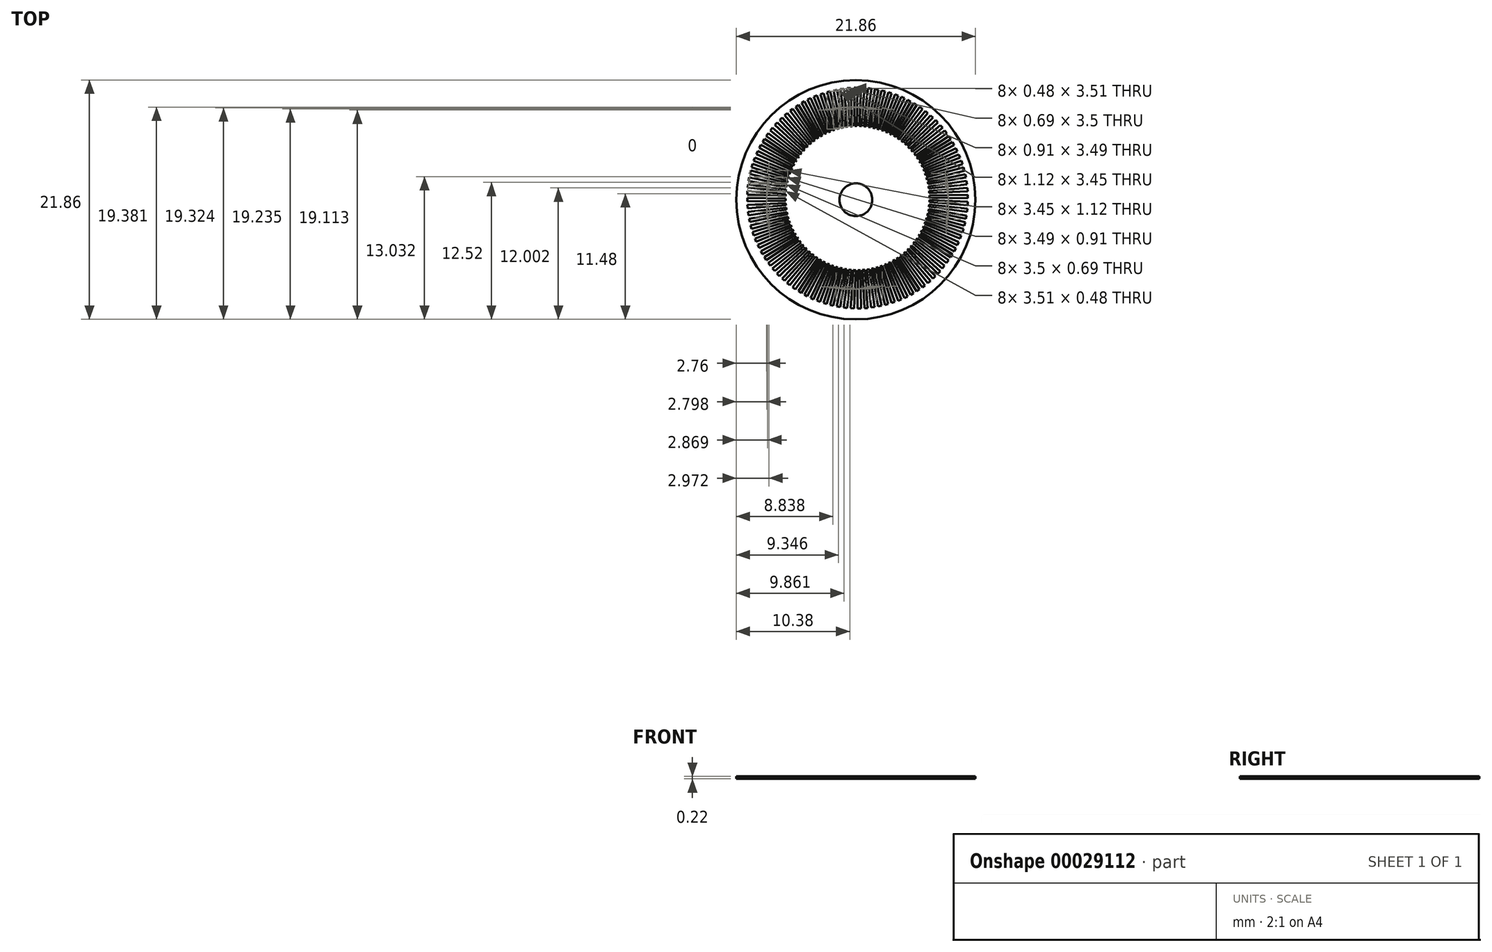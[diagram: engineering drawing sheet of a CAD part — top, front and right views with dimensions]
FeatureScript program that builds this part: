
annotation { "Feature Type Name" : "Feature", "Feature Type Description" : "" }
export const myFeature = defineFeature(function(context is Context, id is Id, definition is map)
    precondition{}
    {
        {
            var Q0;
            Q0=qCreatedBy(makeId("Top.planeOp"),FACE);
            var sketch = newSketch(context, id + "F0", { "sketchPlane" : qUnion([Q0])});
            skCircle(sketch, "E0", {"center": v(0, 0) * mm, "radius": 1.5 * mm});
            skCircle(sketch, "E1", {"center": v(0, 0) * mm, "radius": 10.93 * mm});
            skLineSegment(sketch, "E2", {"start": v(-0.16, 10.23) * mm, "end": v(0.16, 10.23) * mm});
            skLineSegment(sketch, "E3", {"start": v(-0.1, 6.73) * mm, "end": v(0.1, 6.73) * mm});
            skLineSegment(sketch, "E4.trimOffspring", {"start": v(0.1, 6.73) * mm, "end": v(0.16, 10.23) * mm});
            skLineSegment(sketch, "E5.trimOffspring", {"start": v(-0.1, 6.73) * mm, "end": v(-0.16, 10.23) * mm});
            skLineSegment(sketch, "E6.1.0", {"start": v(-0.79, 10.19) * mm, "end": v(-0.48, 10.2) * mm});
            skLineSegment(sketch, "E6.1.1", {"start": v(-0.31, 6.7) * mm, "end": v(-0.48, 10.2) * mm});
            skLineSegment(sketch, "E6.1.2", {"start": v(-0.51, 6.7) * mm, "end": v(-0.79, 10.19) * mm});
            skLineSegment(sketch, "E6.1.3", {"start": v(-0.51, 6.7) * mm, "end": v(-0.31, 6.7) * mm});
            skLineSegment(sketch, "E6.2.0", {"start": v(-1.42, 10.1) * mm, "end": v(-1.1, 10.15) * mm});
            skLineSegment(sketch, "E6.2.1", {"start": v(-0.72, 6.67) * mm, "end": v(-1.1, 10.15) * mm});
            skLineSegment(sketch, "E6.2.2", {"start": v(-0.92, 6.64) * mm, "end": v(-1.42, 10.1) * mm});
            skLineSegment(sketch, "E6.2.3", {"start": v(-0.92, 6.64) * mm, "end": v(-0.72, 6.67) * mm});
            skLineSegment(sketch, "E6.3.0", {"start": v(-2.04, 9.99) * mm, "end": v(-1.73, 10.05) * mm});
            skLineSegment(sketch, "E6.3.1", {"start": v(-1.13, 6.6) * mm, "end": v(-1.73, 10.05) * mm});
            skLineSegment(sketch, "E6.3.2", {"start": v(-1.33, 6.56) * mm, "end": v(-2.04, 9.99) * mm});
            skLineSegment(sketch, "E6.3.3", {"start": v(-1.33, 6.56) * mm, "end": v(-1.13, 6.6) * mm});
            skLineSegment(sketch, "E6.4.0", {"start": v(-2.65, 9.83) * mm, "end": v(-2.35, 9.9) * mm});
            skLineSegment(sketch, "E6.4.1", {"start": v(-1.53, 6.5) * mm, "end": v(-2.35, 9.9) * mm});
            skLineSegment(sketch, "E6.4.2", {"start": v(-1.73, 6.46) * mm, "end": v(-2.65, 9.83) * mm});
            skLineSegment(sketch, "E6.4.3", {"start": v(-1.73, 6.46) * mm, "end": v(-1.53, 6.5) * mm});
            skLineSegment(sketch, "E6.5.0", {"start": v(-3.25, 9.64) * mm, "end": v(-2.96, 9.73) * mm});
            skLineSegment(sketch, "E6.5.1", {"start": v(-1.93, 6.39) * mm, "end": v(-2.96, 9.73) * mm});
            skLineSegment(sketch, "E6.5.2", {"start": v(-2.12, 6.33) * mm, "end": v(-3.25, 9.64) * mm});
            skLineSegment(sketch, "E6.5.3", {"start": v(-2.12, 6.33) * mm, "end": v(-1.93, 6.39) * mm});
            skLineSegment(sketch, "E6.6.0", {"start": v(-3.84, 9.4) * mm, "end": v(-3.55, 9.52) * mm});
            skLineSegment(sketch, "E6.6.1", {"start": v(-2.32, 6.25) * mm, "end": v(-3.55, 9.52) * mm});
            skLineSegment(sketch, "E6.6.2", {"start": v(-2.5, 6.17) * mm, "end": v(-3.84, 9.4) * mm});
            skLineSegment(sketch, "E6.6.3", {"start": v(-2.5, 6.17) * mm, "end": v(-2.32, 6.25) * mm});
            skLineSegment(sketch, "E6.7.0", {"start": v(-4.42, 9.14) * mm, "end": v(-4.13, 9.27) * mm});
            skLineSegment(sketch, "E6.7.1", {"start": v(-2.7, 6.08) * mm, "end": v(-4.13, 9.27) * mm});
            skLineSegment(sketch, "E6.7.2", {"start": v(-2.88, 6) * mm, "end": v(-4.42, 9.14) * mm});
            skLineSegment(sketch, "E6.7.3", {"start": v(-2.88, 6) * mm, "end": v(-2.7, 6.08) * mm});
            skLineSegment(sketch, "E6.8.0", {"start": v(-4.97, 8.83) * mm, "end": v(-4.7, 8.98) * mm});
            skLineSegment(sketch, "E6.8.1", {"start": v(-3.06, 5.89) * mm, "end": v(-4.7, 8.98) * mm});
            skLineSegment(sketch, "E6.8.2", {"start": v(-3.24, 5.8) * mm, "end": v(-4.97, 8.83) * mm});
            skLineSegment(sketch, "E6.8.3", {"start": v(-3.24, 5.8) * mm, "end": v(-3.06, 5.89) * mm});
            skLineSegment(sketch, "E6.9.0", {"start": v(-5.5, 8.5) * mm, "end": v(-5.24, 8.66) * mm});
            skLineSegment(sketch, "E6.9.1", {"start": v(-3.41, 5.68) * mm, "end": v(-5.24, 8.66) * mm});
            skLineSegment(sketch, "E6.9.2", {"start": v(-3.58, 5.57) * mm, "end": v(-5.5, 8.5) * mm});
            skLineSegment(sketch, "E6.9.3", {"start": v(-3.58, 5.57) * mm, "end": v(-3.41, 5.68) * mm});
            skLineSegment(sketch, "E6.10.0", {"start": v(-6.02, 8.12) * mm, "end": v(-5.77, 8.3) * mm});
            skLineSegment(sketch, "E6.10.1", {"start": v(-3.75, 5.44) * mm, "end": v(-5.77, 8.3) * mm});
            skLineSegment(sketch, "E6.10.2", {"start": v(-3.92, 5.32) * mm, "end": v(-6.02, 8.12) * mm});
            skLineSegment(sketch, "E6.10.3", {"start": v(-3.92, 5.32) * mm, "end": v(-3.75, 5.44) * mm});
            skLineSegment(sketch, "E6.11.0", {"start": v(-6.5, 7.72) * mm, "end": v(-6.27, 7.92) * mm});
            skLineSegment(sketch, "E6.11.1", {"start": v(-4.08, 5.18) * mm, "end": v(-6.27, 7.92) * mm});
            skLineSegment(sketch, "E6.11.2", {"start": v(-4.23, 5.06) * mm, "end": v(-6.5, 7.72) * mm});
            skLineSegment(sketch, "E6.11.3", {"start": v(-4.23, 5.06) * mm, "end": v(-4.08, 5.18) * mm});
            skLineSegment(sketch, "E6.12.0", {"start": v(-6.97, 7.28) * mm, "end": v(-6.74, 7.5) * mm});
            skLineSegment(sketch, "E6.12.1", {"start": v(-4.39, 4.9) * mm, "end": v(-6.74, 7.5) * mm});
            skLineSegment(sketch, "E6.12.2", {"start": v(-4.53, 4.77) * mm, "end": v(-6.97, 7.28) * mm});
            skLineSegment(sketch, "E6.12.3", {"start": v(-4.53, 4.77) * mm, "end": v(-4.39, 4.9) * mm});
            skLineSegment(sketch, "E6.13.0", {"start": v(-7.4, 6.82) * mm, "end": v(-7.2, 7.05) * mm});
            skLineSegment(sketch, "E6.13.1", {"start": v(-4.68, 4.62) * mm, "end": v(-7.2, 7.05) * mm});
            skLineSegment(sketch, "E6.13.2", {"start": v(-4.81, 4.47) * mm, "end": v(-7.4, 6.82) * mm});
            skLineSegment(sketch, "E6.13.3", {"start": v(-4.81, 4.47) * mm, "end": v(-4.68, 4.62) * mm});
            skLineSegment(sketch, "E6.14.0", {"start": v(-7.8, 6.34) * mm, "end": v(-7.6, 6.58) * mm});
            skLineSegment(sketch, "E6.14.1", {"start": v(-4.95, 4.3) * mm, "end": v(-7.6, 6.58) * mm});
            skLineSegment(sketch, "E6.14.2", {"start": v(-5.08, 4.15) * mm, "end": v(-7.8, 6.34) * mm});
            skLineSegment(sketch, "E6.14.3", {"start": v(-5.08, 4.15) * mm, "end": v(-4.95, 4.3) * mm});
            skLineSegment(sketch, "E6.15.0", {"start": v(-8.18, 5.82) * mm, "end": v(-8, 6.08) * mm});
            skLineSegment(sketch, "E6.15.1", {"start": v(-5.2, 3.97) * mm, "end": v(-8, 6.08) * mm});
            skLineSegment(sketch, "E6.15.2", {"start": v(-5.32, 3.81) * mm, "end": v(-8.18, 5.82) * mm});
            skLineSegment(sketch, "E6.15.3", {"start": v(-5.32, 3.81) * mm, "end": v(-5.2, 3.97) * mm});
            skLineSegment(sketch, "E6.16.0", {"start": v(-8.52, 5.3) * mm, "end": v(-8.35, 5.55) * mm});
            skLineSegment(sketch, "E6.16.1", {"start": v(-5.43, 3.63) * mm, "end": v(-8.35, 5.55) * mm});
            skLineSegment(sketch, "E6.16.2", {"start": v(-5.54, 3.46) * mm, "end": v(-8.52, 5.3) * mm});
            skLineSegment(sketch, "E6.16.3", {"start": v(-5.54, 3.46) * mm, "end": v(-5.43, 3.63) * mm});
            skLineSegment(sketch, "E6.17.0", {"start": v(-8.83, 4.74) * mm, "end": v(-8.68, 5) * mm});
            skLineSegment(sketch, "E6.17.1", {"start": v(-5.64, 3.27) * mm, "end": v(-8.68, 5) * mm});
            skLineSegment(sketch, "E6.17.2", {"start": v(-5.73, 3.1) * mm, "end": v(-8.83, 4.74) * mm});
            skLineSegment(sketch, "E6.17.3", {"start": v(-5.73, 3.1) * mm, "end": v(-5.64, 3.27) * mm});
            skLineSegment(sketch, "E6.18.0", {"start": v(-9.1, 4.16) * mm, "end": v(-8.96, 4.45) * mm});
            skLineSegment(sketch, "E6.18.1", {"start": v(-5.82, 2.9) * mm, "end": v(-8.96, 4.45) * mm});
            skLineSegment(sketch, "E6.18.2", {"start": v(-5.9, 2.72) * mm, "end": v(-9.1, 4.16) * mm});
            skLineSegment(sketch, "E6.18.3", {"start": v(-5.9, 2.72) * mm, "end": v(-5.82, 2.9) * mm});
            skLineSegment(sketch, "E6.19.0", {"start": v(-9.33, 3.57) * mm, "end": v(-9.22, 3.86) * mm});
            skLineSegment(sketch, "E6.19.1", {"start": v(-5.98, 2.52) * mm, "end": v(-9.22, 3.86) * mm});
            skLineSegment(sketch, "E6.19.2", {"start": v(-6.06, 2.34) * mm, "end": v(-9.33, 3.57) * mm});
            skLineSegment(sketch, "E6.19.3", {"start": v(-6.06, 2.34) * mm, "end": v(-5.98, 2.52) * mm});
            skLineSegment(sketch, "E6.20.0", {"start": v(-9.53, 2.97) * mm, "end": v(-9.43, 3.27) * mm});
            skLineSegment(sketch, "E6.20.1", {"start": v(-6.12, 2.14) * mm, "end": v(-9.43, 3.27) * mm});
            skLineSegment(sketch, "E6.20.2", {"start": v(-6.18, 1.94) * mm, "end": v(-9.53, 2.97) * mm});
            skLineSegment(sketch, "E6.20.3", {"start": v(-6.18, 1.94) * mm, "end": v(-6.12, 2.14) * mm});
            skLineSegment(sketch, "E6.21.0", {"start": v(-9.68, 2.36) * mm, "end": v(-9.6, 2.66) * mm});
            skLineSegment(sketch, "E6.21.1", {"start": v(-6.23, 1.74) * mm, "end": v(-9.6, 2.66) * mm});
            skLineSegment(sketch, "E6.21.2", {"start": v(-6.28, 1.54) * mm, "end": v(-9.68, 2.36) * mm});
            skLineSegment(sketch, "E6.21.3", {"start": v(-6.28, 1.54) * mm, "end": v(-6.23, 1.74) * mm});
            skLineSegment(sketch, "E6.22.0", {"start": v(-9.8, 1.74) * mm, "end": v(-9.75, 2.04) * mm});
            skLineSegment(sketch, "E6.22.1", {"start": v(-6.32, 1.33) * mm, "end": v(-9.75, 2.04) * mm});
            skLineSegment(sketch, "E6.22.2", {"start": v(-6.36, 1.14) * mm, "end": v(-9.8, 1.74) * mm});
            skLineSegment(sketch, "E6.22.3", {"start": v(-6.36, 1.14) * mm, "end": v(-6.32, 1.33) * mm});
            skLineSegment(sketch, "E6.23.0", {"start": v(-9.88, 1.1) * mm, "end": v(-9.84, 1.42) * mm});
            skLineSegment(sketch, "E6.23.1", {"start": v(-6.38, 0.93) * mm, "end": v(-9.84, 1.42) * mm});
            skLineSegment(sketch, "E6.23.2", {"start": v(-6.4, 0.73) * mm, "end": v(-9.88, 1.1) * mm});
            skLineSegment(sketch, "E6.23.3", {"start": v(-6.4, 0.73) * mm, "end": v(-6.38, 0.93) * mm});
            skLineSegment(sketch, "E6.24.0", {"start": v(-9.92, 0.48) * mm, "end": v(-9.9, 0.79) * mm});
            skLineSegment(sketch, "E6.24.1", {"start": v(-6.42, 0.51) * mm, "end": v(-9.9, 0.79) * mm});
            skLineSegment(sketch, "E6.24.2", {"start": v(-6.43, 0.31) * mm, "end": v(-9.92, 0.48) * mm});
            skLineSegment(sketch, "E6.24.3", {"start": v(-6.43, 0.31) * mm, "end": v(-6.42, 0.51) * mm});
            skLineSegment(sketch, "E6.25.0", {"start": v(-9.92, -0.16) * mm, "end": v(-9.92, 0.16) * mm});
            skLineSegment(sketch, "E6.25.1", {"start": v(-6.42, 0.1) * mm, "end": v(-9.92, 0.16) * mm});
            skLineSegment(sketch, "E6.25.2", {"start": v(-6.43, -0.1) * mm, "end": v(-9.93, -0.16) * mm});
            skLineSegment(sketch, "E6.25.3", {"start": v(-6.43, -0.1) * mm, "end": v(-6.43, 0.1) * mm});
            skLineSegment(sketch, "E6.26.0", {"start": v(-9.89, -0.79) * mm, "end": v(-9.9, -0.48) * mm});
            skLineSegment(sketch, "E6.26.1", {"start": v(-6.4, -0.31) * mm, "end": v(-9.9, -0.48) * mm});
            skLineSegment(sketch, "E6.26.2", {"start": v(-6.4, -0.51) * mm, "end": v(-9.89, -0.79) * mm});
            skLineSegment(sketch, "E6.26.3", {"start": v(-6.4, -0.51) * mm, "end": v(-6.4, -0.31) * mm});
            skLineSegment(sketch, "E6.27.0", {"start": v(-9.8, -1.42) * mm, "end": v(-9.85, -1.1) * mm});
            skLineSegment(sketch, "E6.27.1", {"start": v(-6.37, -0.72) * mm, "end": v(-9.85, -1.1) * mm});
            skLineSegment(sketch, "E6.27.2", {"start": v(-6.34, -0.92) * mm, "end": v(-9.8, -1.42) * mm});
            skLineSegment(sketch, "E6.27.3", {"start": v(-6.34, -0.92) * mm, "end": v(-6.37, -0.72) * mm});
            skLineSegment(sketch, "E6.28.0", {"start": v(-9.69, -2.04) * mm, "end": v(-9.75, -1.73) * mm});
            skLineSegment(sketch, "E6.28.1", {"start": v(-6.3, -1.13) * mm, "end": v(-9.75, -1.73) * mm});
            skLineSegment(sketch, "E6.28.2", {"start": v(-6.26, -1.33) * mm, "end": v(-9.69, -2.04) * mm});
            skLineSegment(sketch, "E6.28.3", {"start": v(-6.26, -1.33) * mm, "end": v(-6.3, -1.13) * mm});
            skLineSegment(sketch, "E6.29.0", {"start": v(-9.53, -2.65) * mm, "end": v(-9.6, -2.35) * mm});
            skLineSegment(sketch, "E6.29.1", {"start": v(-6.2, -1.53) * mm, "end": v(-9.6, -2.35) * mm});
            skLineSegment(sketch, "E6.29.2", {"start": v(-6.16, -1.73) * mm, "end": v(-9.53, -2.65) * mm});
            skLineSegment(sketch, "E6.29.3", {"start": v(-6.16, -1.73) * mm, "end": v(-6.2, -1.53) * mm});
            skLineSegment(sketch, "E6.30.0", {"start": v(-9.34, -3.25) * mm, "end": v(-9.43, -2.96) * mm});
            skLineSegment(sketch, "E6.30.1", {"start": v(-6.09, -1.93) * mm, "end": v(-9.43, -2.96) * mm});
            skLineSegment(sketch, "E6.30.2", {"start": v(-6.03, -2.12) * mm, "end": v(-9.34, -3.25) * mm});
            skLineSegment(sketch, "E6.30.3", {"start": v(-6.03, -2.12) * mm, "end": v(-6.09, -1.93) * mm});
            skLineSegment(sketch, "E6.31.0", {"start": v(-9.1, -3.84) * mm, "end": v(-9.22, -3.55) * mm});
            skLineSegment(sketch, "E6.31.1", {"start": v(-5.95, -2.32) * mm, "end": v(-9.22, -3.55) * mm});
            skLineSegment(sketch, "E6.31.2", {"start": v(-5.87, -2.5) * mm, "end": v(-9.1, -3.84) * mm});
            skLineSegment(sketch, "E6.31.3", {"start": v(-5.87, -2.5) * mm, "end": v(-5.95, -2.32) * mm});
            skLineSegment(sketch, "E6.32.0", {"start": v(-8.84, -4.42) * mm, "end": v(-8.97, -4.13) * mm});
            skLineSegment(sketch, "E6.32.1", {"start": v(-5.78, -2.7) * mm, "end": v(-8.97, -4.13) * mm});
            skLineSegment(sketch, "E6.32.2", {"start": v(-5.7, -2.88) * mm, "end": v(-8.84, -4.42) * mm});
            skLineSegment(sketch, "E6.32.3", {"start": v(-5.7, -2.88) * mm, "end": v(-5.78, -2.7) * mm});
            skLineSegment(sketch, "E6.33.0", {"start": v(-8.53, -4.97) * mm, "end": v(-8.68, -4.7) * mm});
            skLineSegment(sketch, "E6.33.1", {"start": v(-5.59, -3.06) * mm, "end": v(-8.68, -4.7) * mm});
            skLineSegment(sketch, "E6.33.2", {"start": v(-5.5, -3.24) * mm, "end": v(-8.53, -4.97) * mm});
            skLineSegment(sketch, "E6.33.3", {"start": v(-5.5, -3.24) * mm, "end": v(-5.59, -3.06) * mm});
            skLineSegment(sketch, "E6.34.0", {"start": v(-8.2, -5.5) * mm, "end": v(-8.36, -5.24) * mm});
            skLineSegment(sketch, "E6.34.1", {"start": v(-5.38, -3.41) * mm, "end": v(-8.36, -5.24) * mm});
            skLineSegment(sketch, "E6.34.2", {"start": v(-5.27, -3.58) * mm, "end": v(-8.2, -5.5) * mm});
            skLineSegment(sketch, "E6.34.3", {"start": v(-5.27, -3.58) * mm, "end": v(-5.38, -3.41) * mm});
            skLineSegment(sketch, "E6.35.0", {"start": v(-7.82, -6.02) * mm, "end": v(-8, -5.77) * mm});
            skLineSegment(sketch, "E6.35.1", {"start": v(-5.14, -3.75) * mm, "end": v(-8, -5.77) * mm});
            skLineSegment(sketch, "E6.35.2", {"start": v(-5.02, -3.92) * mm, "end": v(-7.82, -6.02) * mm});
            skLineSegment(sketch, "E6.35.3", {"start": v(-5.02, -3.92) * mm, "end": v(-5.14, -3.75) * mm});
            skLineSegment(sketch, "E6.36.0", {"start": v(-7.42, -6.5) * mm, "end": v(-7.62, -6.27) * mm});
            skLineSegment(sketch, "E6.36.1", {"start": v(-4.88, -4.08) * mm, "end": v(-7.62, -6.27) * mm});
            skLineSegment(sketch, "E6.36.2", {"start": v(-4.76, -4.23) * mm, "end": v(-7.42, -6.5) * mm});
            skLineSegment(sketch, "E6.36.3", {"start": v(-4.76, -4.23) * mm, "end": v(-4.88, -4.08) * mm});
            skLineSegment(sketch, "E6.37.0", {"start": v(-6.98, -6.97) * mm, "end": v(-7.2, -6.74) * mm});
            skLineSegment(sketch, "E6.37.1", {"start": v(-4.6, -4.39) * mm, "end": v(-7.2, -6.74) * mm});
            skLineSegment(sketch, "E6.37.2", {"start": v(-4.47, -4.53) * mm, "end": v(-6.98, -6.97) * mm});
            skLineSegment(sketch, "E6.37.3", {"start": v(-4.47, -4.53) * mm, "end": v(-4.6, -4.39) * mm});
            skLineSegment(sketch, "E6.38.0", {"start": v(-6.52, -7.4) * mm, "end": v(-6.75, -7.2) * mm});
            skLineSegment(sketch, "E6.38.1", {"start": v(-4.32, -4.68) * mm, "end": v(-6.75, -7.2) * mm});
            skLineSegment(sketch, "E6.38.2", {"start": v(-4.17, -4.81) * mm, "end": v(-6.52, -7.4) * mm});
            skLineSegment(sketch, "E6.38.3", {"start": v(-4.17, -4.81) * mm, "end": v(-4.32, -4.68) * mm});
            skLineSegment(sketch, "E6.39.0", {"start": v(-6.04, -7.8) * mm, "end": v(-6.28, -7.6) * mm});
            skLineSegment(sketch, "E6.39.1", {"start": v(-4, -4.95) * mm, "end": v(-6.28, -7.6) * mm});
            skLineSegment(sketch, "E6.39.2", {"start": v(-3.85, -5.08) * mm, "end": v(-6.04, -7.8) * mm});
            skLineSegment(sketch, "E6.39.3", {"start": v(-3.85, -5.08) * mm, "end": v(-4, -4.95) * mm});
            skLineSegment(sketch, "E6.40.0", {"start": v(-5.52, -8.18) * mm, "end": v(-5.78, -8) * mm});
            skLineSegment(sketch, "E6.40.1", {"start": v(-3.67, -5.2) * mm, "end": v(-5.78, -8) * mm});
            skLineSegment(sketch, "E6.40.2", {"start": v(-3.51, -5.32) * mm, "end": v(-5.52, -8.18) * mm});
            skLineSegment(sketch, "E6.40.3", {"start": v(-3.51, -5.32) * mm, "end": v(-3.67, -5.2) * mm});
            skLineSegment(sketch, "E6.41.0", {"start": v(-5, -8.52) * mm, "end": v(-5.25, -8.35) * mm});
            skLineSegment(sketch, "E6.41.1", {"start": v(-3.33, -5.43) * mm, "end": v(-5.25, -8.35) * mm});
            skLineSegment(sketch, "E6.41.2", {"start": v(-3.16, -5.54) * mm, "end": v(-5, -8.52) * mm});
            skLineSegment(sketch, "E6.41.3", {"start": v(-3.16, -5.54) * mm, "end": v(-3.33, -5.43) * mm});
            skLineSegment(sketch, "E6.42.0", {"start": v(-4.44, -8.83) * mm, "end": v(-4.7, -8.68) * mm});
            skLineSegment(sketch, "E6.42.1", {"start": v(-2.97, -5.64) * mm, "end": v(-4.7, -8.68) * mm});
            skLineSegment(sketch, "E6.42.2", {"start": v(-2.8, -5.73) * mm, "end": v(-4.44, -8.83) * mm});
            skLineSegment(sketch, "E6.42.3", {"start": v(-2.8, -5.73) * mm, "end": v(-2.97, -5.64) * mm});
            skLineSegment(sketch, "E6.43.0", {"start": v(-3.86, -9.1) * mm, "end": v(-4.15, -8.96) * mm});
            skLineSegment(sketch, "E6.43.1", {"start": v(-2.6, -5.82) * mm, "end": v(-4.15, -8.96) * mm});
            skLineSegment(sketch, "E6.43.2", {"start": v(-2.42, -5.9) * mm, "end": v(-3.86, -9.1) * mm});
            skLineSegment(sketch, "E6.43.3", {"start": v(-2.42, -5.9) * mm, "end": v(-2.6, -5.82) * mm});
            skLineSegment(sketch, "E6.44.0", {"start": v(-3.27, -9.33) * mm, "end": v(-3.56, -9.22) * mm});
            skLineSegment(sketch, "E6.44.1", {"start": v(-2.22, -5.98) * mm, "end": v(-3.56, -9.22) * mm});
            skLineSegment(sketch, "E6.44.2", {"start": v(-2.04, -6.06) * mm, "end": v(-3.27, -9.33) * mm});
            skLineSegment(sketch, "E6.44.3", {"start": v(-2.04, -6.06) * mm, "end": v(-2.22, -5.98) * mm});
            skLineSegment(sketch, "E6.45.0", {"start": v(-2.67, -9.53) * mm, "end": v(-2.97, -9.43) * mm});
            skLineSegment(sketch, "E6.45.1", {"start": v(-1.84, -6.12) * mm, "end": v(-2.97, -9.43) * mm});
            skLineSegment(sketch, "E6.45.2", {"start": v(-1.64, -6.18) * mm, "end": v(-2.67, -9.53) * mm});
            skLineSegment(sketch, "E6.45.3", {"start": v(-1.64, -6.18) * mm, "end": v(-1.84, -6.12) * mm});
            skLineSegment(sketch, "E6.46.0", {"start": v(-2.06, -9.68) * mm, "end": v(-2.36, -9.6) * mm});
            skLineSegment(sketch, "E6.46.1", {"start": v(-1.44, -6.23) * mm, "end": v(-2.36, -9.6) * mm});
            skLineSegment(sketch, "E6.46.2", {"start": v(-1.24, -6.28) * mm, "end": v(-2.06, -9.68) * mm});
            skLineSegment(sketch, "E6.46.3", {"start": v(-1.24, -6.28) * mm, "end": v(-1.44, -6.23) * mm});
            skLineSegment(sketch, "E6.47.0", {"start": v(-1.44, -9.8) * mm, "end": v(-1.74, -9.75) * mm});
            skLineSegment(sketch, "E6.47.1", {"start": v(-1.03, -6.32) * mm, "end": v(-1.74, -9.75) * mm});
            skLineSegment(sketch, "E6.47.2", {"start": v(-0.84, -6.36) * mm, "end": v(-1.44, -9.8) * mm});
            skLineSegment(sketch, "E6.47.3", {"start": v(-0.84, -6.36) * mm, "end": v(-1.03, -6.32) * mm});
            skLineSegment(sketch, "E6.48.0", {"start": v(-0.8, -9.88) * mm, "end": v(-1.12, -9.84) * mm});
            skLineSegment(sketch, "E6.48.1", {"start": v(-0.63, -6.38) * mm, "end": v(-1.12, -9.84) * mm});
            skLineSegment(sketch, "E6.48.2", {"start": v(-0.43, -6.4) * mm, "end": v(-0.8, -9.88) * mm});
            skLineSegment(sketch, "E6.48.3", {"start": v(-0.43, -6.4) * mm, "end": v(-0.63, -6.38) * mm});
            skLineSegment(sketch, "E6.49.0", {"start": v(-0.18, -9.92) * mm, "end": v(-0.49, -9.9) * mm});
            skLineSegment(sketch, "E6.49.1", {"start": v(-0.21, -6.42) * mm, "end": v(-0.49, -9.9) * mm});
            skLineSegment(sketch, "E6.49.2", {"start": v(-0.01, -6.43) * mm, "end": v(-0.18, -9.92) * mm});
            skLineSegment(sketch, "E6.49.3", {"start": v(-0.01, -6.43) * mm, "end": v(-0.21, -6.42) * mm});
            skLineSegment(sketch, "E6.50.0", {"start": v(0.46, -9.93) * mm, "end": v(0.14, -9.93) * mm});
            skLineSegment(sketch, "E6.50.1", {"start": v(0.2, -6.43) * mm, "end": v(0.14, -9.93) * mm});
            skLineSegment(sketch, "E6.50.2", {"start": v(0.4, -6.43) * mm, "end": v(0.46, -9.93) * mm});
            skLineSegment(sketch, "E6.50.3", {"start": v(0.4, -6.43) * mm, "end": v(0.2, -6.43) * mm});
            skLineSegment(sketch, "E6.51.0", {"start": v(1.09, -9.89) * mm, "end": v(0.78, -9.9) * mm});
            skLineSegment(sketch, "E6.51.1", {"start": v(0.61, -6.4) * mm, "end": v(0.78, -9.9) * mm});
            skLineSegment(sketch, "E6.51.2", {"start": v(0.81, -6.4) * mm, "end": v(1.09, -9.89) * mm});
            skLineSegment(sketch, "E6.51.3", {"start": v(0.81, -6.4) * mm, "end": v(0.61, -6.4) * mm});
            skLineSegment(sketch, "E6.52.0", {"start": v(1.72, -9.8) * mm, "end": v(1.4, -9.85) * mm});
            skLineSegment(sketch, "E6.52.1", {"start": v(1.02, -6.37) * mm, "end": v(1.4, -9.85) * mm});
            skLineSegment(sketch, "E6.52.2", {"start": v(1.22, -6.34) * mm, "end": v(1.72, -9.8) * mm});
            skLineSegment(sketch, "E6.52.3", {"start": v(1.22, -6.34) * mm, "end": v(1.02, -6.37) * mm});
            skLineSegment(sketch, "E6.53.0", {"start": v(2.34, -9.69) * mm, "end": v(2.03, -9.75) * mm});
            skLineSegment(sketch, "E6.53.1", {"start": v(1.43, -6.3) * mm, "end": v(2.03, -9.75) * mm});
            skLineSegment(sketch, "E6.53.2", {"start": v(1.63, -6.26) * mm, "end": v(2.34, -9.69) * mm});
            skLineSegment(sketch, "E6.53.3", {"start": v(1.63, -6.26) * mm, "end": v(1.43, -6.3) * mm});
            skLineSegment(sketch, "E6.54.0", {"start": v(2.95, -9.53) * mm, "end": v(2.65, -9.6) * mm});
            skLineSegment(sketch, "E6.54.1", {"start": v(1.83, -6.2) * mm, "end": v(2.65, -9.6) * mm});
            skLineSegment(sketch, "E6.54.2", {"start": v(2.03, -6.16) * mm, "end": v(2.95, -9.53) * mm});
            skLineSegment(sketch, "E6.54.3", {"start": v(2.03, -6.16) * mm, "end": v(1.83, -6.2) * mm});
            skLineSegment(sketch, "E6.55.0", {"start": v(3.55, -9.34) * mm, "end": v(3.26, -9.43) * mm});
            skLineSegment(sketch, "E6.55.1", {"start": v(2.23, -6.09) * mm, "end": v(3.26, -9.43) * mm});
            skLineSegment(sketch, "E6.55.2", {"start": v(2.42, -6.03) * mm, "end": v(3.55, -9.34) * mm});
            skLineSegment(sketch, "E6.55.3", {"start": v(2.42, -6.03) * mm, "end": v(2.23, -6.09) * mm});
            skLineSegment(sketch, "E6.56.0", {"start": v(4.14, -9.1) * mm, "end": v(3.85, -9.22) * mm});
            skLineSegment(sketch, "E6.56.1", {"start": v(2.62, -5.95) * mm, "end": v(3.85, -9.22) * mm});
            skLineSegment(sketch, "E6.56.2", {"start": v(2.8, -5.87) * mm, "end": v(4.14, -9.1) * mm});
            skLineSegment(sketch, "E6.56.3", {"start": v(2.8, -5.87) * mm, "end": v(2.62, -5.95) * mm});
            skLineSegment(sketch, "E6.57.0", {"start": v(4.72, -8.84) * mm, "end": v(4.43, -8.97) * mm});
            skLineSegment(sketch, "E6.57.1", {"start": v(3, -5.78) * mm, "end": v(4.43, -8.97) * mm});
            skLineSegment(sketch, "E6.57.2", {"start": v(3.18, -5.7) * mm, "end": v(4.72, -8.84) * mm});
            skLineSegment(sketch, "E6.57.3", {"start": v(3.18, -5.7) * mm, "end": v(3, -5.78) * mm});
            skLineSegment(sketch, "E6.58.0", {"start": v(5.27, -8.53) * mm, "end": v(5, -8.68) * mm});
            skLineSegment(sketch, "E6.58.1", {"start": v(3.36, -5.59) * mm, "end": v(5, -8.68) * mm});
            skLineSegment(sketch, "E6.58.2", {"start": v(3.54, -5.5) * mm, "end": v(5.27, -8.53) * mm});
            skLineSegment(sketch, "E6.58.3", {"start": v(3.54, -5.5) * mm, "end": v(3.36, -5.59) * mm});
            skLineSegment(sketch, "E6.59.0", {"start": v(5.8, -8.2) * mm, "end": v(5.54, -8.36) * mm});
            skLineSegment(sketch, "E6.59.1", {"start": v(3.71, -5.38) * mm, "end": v(5.54, -8.36) * mm});
            skLineSegment(sketch, "E6.59.2", {"start": v(3.88, -5.27) * mm, "end": v(5.8, -8.2) * mm});
            skLineSegment(sketch, "E6.59.3", {"start": v(3.88, -5.27) * mm, "end": v(3.71, -5.38) * mm});
            skLineSegment(sketch, "E6.60.0", {"start": v(6.32, -7.82) * mm, "end": v(6.07, -8) * mm});
            skLineSegment(sketch, "E6.60.1", {"start": v(4.05, -5.14) * mm, "end": v(6.07, -8) * mm});
            skLineSegment(sketch, "E6.60.2", {"start": v(4.22, -5.02) * mm, "end": v(6.32, -7.82) * mm});
            skLineSegment(sketch, "E6.60.3", {"start": v(4.22, -5.02) * mm, "end": v(4.05, -5.14) * mm});
            skLineSegment(sketch, "E6.61.0", {"start": v(6.8, -7.42) * mm, "end": v(6.57, -7.62) * mm});
            skLineSegment(sketch, "E6.61.1", {"start": v(4.38, -4.88) * mm, "end": v(6.57, -7.62) * mm});
            skLineSegment(sketch, "E6.61.2", {"start": v(4.53, -4.76) * mm, "end": v(6.8, -7.42) * mm});
            skLineSegment(sketch, "E6.61.3", {"start": v(4.53, -4.76) * mm, "end": v(4.38, -4.88) * mm});
            skLineSegment(sketch, "E6.62.0", {"start": v(7.27, -6.98) * mm, "end": v(7.04, -7.2) * mm});
            skLineSegment(sketch, "E6.62.1", {"start": v(4.69, -4.6) * mm, "end": v(7.04, -7.2) * mm});
            skLineSegment(sketch, "E6.62.2", {"start": v(4.83, -4.47) * mm, "end": v(7.27, -6.98) * mm});
            skLineSegment(sketch, "E6.62.3", {"start": v(4.83, -4.47) * mm, "end": v(4.69, -4.6) * mm});
            skLineSegment(sketch, "E6.63.0", {"start": v(7.7, -6.52) * mm, "end": v(7.5, -6.75) * mm});
            skLineSegment(sketch, "E6.63.1", {"start": v(4.98, -4.32) * mm, "end": v(7.5, -6.75) * mm});
            skLineSegment(sketch, "E6.63.2", {"start": v(5.11, -4.17) * mm, "end": v(7.7, -6.52) * mm});
            skLineSegment(sketch, "E6.63.3", {"start": v(5.11, -4.17) * mm, "end": v(4.98, -4.32) * mm});
            skLineSegment(sketch, "E6.64.0", {"start": v(8.1, -6.04) * mm, "end": v(7.9, -6.28) * mm});
            skLineSegment(sketch, "E6.64.1", {"start": v(5.25, -4) * mm, "end": v(7.9, -6.28) * mm});
            skLineSegment(sketch, "E6.64.2", {"start": v(5.38, -3.85) * mm, "end": v(8.1, -6.04) * mm});
            skLineSegment(sketch, "E6.64.3", {"start": v(5.38, -3.85) * mm, "end": v(5.25, -4) * mm});
            skLineSegment(sketch, "E6.65.0", {"start": v(8.48, -5.52) * mm, "end": v(8.3, -5.78) * mm});
            skLineSegment(sketch, "E6.65.1", {"start": v(5.5, -3.67) * mm, "end": v(8.3, -5.78) * mm});
            skLineSegment(sketch, "E6.65.2", {"start": v(5.62, -3.51) * mm, "end": v(8.48, -5.52) * mm});
            skLineSegment(sketch, "E6.65.3", {"start": v(5.62, -3.51) * mm, "end": v(5.5, -3.67) * mm});
            skLineSegment(sketch, "E6.66.0", {"start": v(8.82, -5) * mm, "end": v(8.65, -5.25) * mm});
            skLineSegment(sketch, "E6.66.1", {"start": v(5.73, -3.33) * mm, "end": v(8.65, -5.25) * mm});
            skLineSegment(sketch, "E6.66.2", {"start": v(5.84, -3.16) * mm, "end": v(8.82, -5) * mm});
            skLineSegment(sketch, "E6.66.3", {"start": v(5.84, -3.16) * mm, "end": v(5.73, -3.33) * mm});
            skLineSegment(sketch, "E6.67.0", {"start": v(9.13, -4.44) * mm, "end": v(8.98, -4.7) * mm});
            skLineSegment(sketch, "E6.67.1", {"start": v(5.94, -2.97) * mm, "end": v(8.98, -4.7) * mm});
            skLineSegment(sketch, "E6.67.2", {"start": v(6.03, -2.8) * mm, "end": v(9.13, -4.44) * mm});
            skLineSegment(sketch, "E6.67.3", {"start": v(6.03, -2.8) * mm, "end": v(5.94, -2.97) * mm});
            skLineSegment(sketch, "E6.68.0", {"start": v(9.4, -3.86) * mm, "end": v(9.26, -4.15) * mm});
            skLineSegment(sketch, "E6.68.1", {"start": v(6.12, -2.6) * mm, "end": v(9.26, -4.15) * mm});
            skLineSegment(sketch, "E6.68.2", {"start": v(6.2, -2.42) * mm, "end": v(9.4, -3.86) * mm});
            skLineSegment(sketch, "E6.68.3", {"start": v(6.2, -2.42) * mm, "end": v(6.12, -2.6) * mm});
            skLineSegment(sketch, "E6.69.0", {"start": v(9.63, -3.27) * mm, "end": v(9.52, -3.56) * mm});
            skLineSegment(sketch, "E6.69.1", {"start": v(6.28, -2.22) * mm, "end": v(9.52, -3.56) * mm});
            skLineSegment(sketch, "E6.69.2", {"start": v(6.36, -2.04) * mm, "end": v(9.63, -3.27) * mm});
            skLineSegment(sketch, "E6.69.3", {"start": v(6.36, -2.04) * mm, "end": v(6.28, -2.22) * mm});
            skLineSegment(sketch, "E6.70.0", {"start": v(9.83, -2.67) * mm, "end": v(9.73, -2.97) * mm});
            skLineSegment(sketch, "E6.70.1", {"start": v(6.42, -1.84) * mm, "end": v(9.73, -2.97) * mm});
            skLineSegment(sketch, "E6.70.2", {"start": v(6.48, -1.64) * mm, "end": v(9.83, -2.67) * mm});
            skLineSegment(sketch, "E6.70.3", {"start": v(6.48, -1.64) * mm, "end": v(6.42, -1.84) * mm});
            skLineSegment(sketch, "E6.71.0", {"start": v(9.98, -2.06) * mm, "end": v(9.9, -2.36) * mm});
            skLineSegment(sketch, "E6.71.1", {"start": v(6.53, -1.44) * mm, "end": v(9.9, -2.36) * mm});
            skLineSegment(sketch, "E6.71.2", {"start": v(6.58, -1.24) * mm, "end": v(9.98, -2.06) * mm});
            skLineSegment(sketch, "E6.71.3", {"start": v(6.58, -1.24) * mm, "end": v(6.53, -1.44) * mm});
            skLineSegment(sketch, "E6.72.0", {"start": v(10.1, -1.44) * mm, "end": v(10.05, -1.74) * mm});
            skLineSegment(sketch, "E6.72.1", {"start": v(6.62, -1.03) * mm, "end": v(10.05, -1.74) * mm});
            skLineSegment(sketch, "E6.72.2", {"start": v(6.66, -0.84) * mm, "end": v(10.1, -1.44) * mm});
            skLineSegment(sketch, "E6.72.3", {"start": v(6.66, -0.84) * mm, "end": v(6.62, -1.03) * mm});
            skLineSegment(sketch, "E6.73.0", {"start": v(10.18, -0.8) * mm, "end": v(10.14, -1.12) * mm});
            skLineSegment(sketch, "E6.73.1", {"start": v(6.68, -0.63) * mm, "end": v(10.14, -1.12) * mm});
            skLineSegment(sketch, "E6.73.2", {"start": v(6.7, -0.43) * mm, "end": v(10.18, -0.8) * mm});
            skLineSegment(sketch, "E6.73.3", {"start": v(6.7, -0.43) * mm, "end": v(6.68, -0.63) * mm});
            skLineSegment(sketch, "E6.74.0", {"start": v(10.22, -0.18) * mm, "end": v(10.2, -0.49) * mm});
            skLineSegment(sketch, "E6.74.1", {"start": v(6.72, -0.21) * mm, "end": v(10.2, -0.49) * mm});
            skLineSegment(sketch, "E6.74.2", {"start": v(6.73, -0.01) * mm, "end": v(10.22, -0.18) * mm});
            skLineSegment(sketch, "E6.74.3", {"start": v(6.73, -0.01) * mm, "end": v(6.72, -0.21) * mm});
            skLineSegment(sketch, "E6.75.0", {"start": v(10.23, 0.46) * mm, "end": v(10.23, 0.14) * mm});
            skLineSegment(sketch, "E6.75.1", {"start": v(6.73, 0.2) * mm, "end": v(10.23, 0.14) * mm});
            skLineSegment(sketch, "E6.75.2", {"start": v(6.73, 0.4) * mm, "end": v(10.23, 0.46) * mm});
            skLineSegment(sketch, "E6.75.3", {"start": v(6.73, 0.4) * mm, "end": v(6.73, 0.2) * mm});
            skLineSegment(sketch, "E6.76.0", {"start": v(10.19, 1.09) * mm, "end": v(10.2, 0.78) * mm});
            skLineSegment(sketch, "E6.76.1", {"start": v(6.7, 0.61) * mm, "end": v(10.2, 0.78) * mm});
            skLineSegment(sketch, "E6.76.2", {"start": v(6.7, 0.81) * mm, "end": v(10.19, 1.09) * mm});
            skLineSegment(sketch, "E6.76.3", {"start": v(6.7, 0.81) * mm, "end": v(6.7, 0.61) * mm});
            skLineSegment(sketch, "E6.77.0", {"start": v(10.1, 1.72) * mm, "end": v(10.15, 1.4) * mm});
            skLineSegment(sketch, "E6.77.1", {"start": v(6.67, 1.02) * mm, "end": v(10.15, 1.4) * mm});
            skLineSegment(sketch, "E6.77.2", {"start": v(6.64, 1.22) * mm, "end": v(10.1, 1.72) * mm});
            skLineSegment(sketch, "E6.77.3", {"start": v(6.64, 1.22) * mm, "end": v(6.67, 1.02) * mm});
            skLineSegment(sketch, "E6.78.0", {"start": v(9.99, 2.34) * mm, "end": v(10.05, 2.03) * mm});
            skLineSegment(sketch, "E6.78.1", {"start": v(6.6, 1.43) * mm, "end": v(10.05, 2.03) * mm});
            skLineSegment(sketch, "E6.78.2", {"start": v(6.56, 1.63) * mm, "end": v(9.99, 2.34) * mm});
            skLineSegment(sketch, "E6.78.3", {"start": v(6.56, 1.63) * mm, "end": v(6.6, 1.43) * mm});
            skLineSegment(sketch, "E6.79.0", {"start": v(9.83, 2.95) * mm, "end": v(9.9, 2.65) * mm});
            skLineSegment(sketch, "E6.79.1", {"start": v(6.5, 1.83) * mm, "end": v(9.9, 2.65) * mm});
            skLineSegment(sketch, "E6.79.2", {"start": v(6.46, 2.03) * mm, "end": v(9.83, 2.95) * mm});
            skLineSegment(sketch, "E6.79.3", {"start": v(6.46, 2.03) * mm, "end": v(6.5, 1.83) * mm});
            skLineSegment(sketch, "E6.80.0", {"start": v(9.64, 3.55) * mm, "end": v(9.73, 3.26) * mm});
            skLineSegment(sketch, "E6.80.1", {"start": v(6.39, 2.23) * mm, "end": v(9.73, 3.26) * mm});
            skLineSegment(sketch, "E6.80.2", {"start": v(6.33, 2.42) * mm, "end": v(9.64, 3.55) * mm});
            skLineSegment(sketch, "E6.80.3", {"start": v(6.33, 2.42) * mm, "end": v(6.39, 2.23) * mm});
            skLineSegment(sketch, "E6.81.0", {"start": v(9.4, 4.14) * mm, "end": v(9.52, 3.85) * mm});
            skLineSegment(sketch, "E6.81.1", {"start": v(6.25, 2.62) * mm, "end": v(9.52, 3.85) * mm});
            skLineSegment(sketch, "E6.81.2", {"start": v(6.17, 2.8) * mm, "end": v(9.4, 4.14) * mm});
            skLineSegment(sketch, "E6.81.3", {"start": v(6.17, 2.8) * mm, "end": v(6.25, 2.62) * mm});
            skLineSegment(sketch, "E6.82.0", {"start": v(9.14, 4.72) * mm, "end": v(9.27, 4.43) * mm});
            skLineSegment(sketch, "E6.82.1", {"start": v(6.08, 3) * mm, "end": v(9.27, 4.43) * mm});
            skLineSegment(sketch, "E6.82.2", {"start": v(6, 3.18) * mm, "end": v(9.14, 4.72) * mm});
            skLineSegment(sketch, "E6.82.3", {"start": v(6, 3.18) * mm, "end": v(6.08, 3) * mm});
            skLineSegment(sketch, "E6.83.0", {"start": v(8.83, 5.27) * mm, "end": v(8.98, 5) * mm});
            skLineSegment(sketch, "E6.83.1", {"start": v(5.89, 3.36) * mm, "end": v(8.98, 5) * mm});
            skLineSegment(sketch, "E6.83.2", {"start": v(5.8, 3.54) * mm, "end": v(8.83, 5.27) * mm});
            skLineSegment(sketch, "E6.83.3", {"start": v(5.8, 3.54) * mm, "end": v(5.89, 3.36) * mm});
            skLineSegment(sketch, "E6.84.0", {"start": v(8.5, 5.8) * mm, "end": v(8.66, 5.54) * mm});
            skLineSegment(sketch, "E6.84.1", {"start": v(5.68, 3.71) * mm, "end": v(8.66, 5.54) * mm});
            skLineSegment(sketch, "E6.84.2", {"start": v(5.57, 3.88) * mm, "end": v(8.5, 5.8) * mm});
            skLineSegment(sketch, "E6.84.3", {"start": v(5.57, 3.88) * mm, "end": v(5.68, 3.71) * mm});
            skLineSegment(sketch, "E6.85.0", {"start": v(8.12, 6.32) * mm, "end": v(8.3, 6.07) * mm});
            skLineSegment(sketch, "E6.85.1", {"start": v(5.44, 4.05) * mm, "end": v(8.3, 6.07) * mm});
            skLineSegment(sketch, "E6.85.2", {"start": v(5.32, 4.22) * mm, "end": v(8.12, 6.32) * mm});
            skLineSegment(sketch, "E6.85.3", {"start": v(5.32, 4.22) * mm, "end": v(5.44, 4.05) * mm});
            skLineSegment(sketch, "E6.86.0", {"start": v(7.72, 6.8) * mm, "end": v(7.92, 6.57) * mm});
            skLineSegment(sketch, "E6.86.1", {"start": v(5.18, 4.38) * mm, "end": v(7.92, 6.57) * mm});
            skLineSegment(sketch, "E6.86.2", {"start": v(5.06, 4.53) * mm, "end": v(7.72, 6.8) * mm});
            skLineSegment(sketch, "E6.86.3", {"start": v(5.06, 4.53) * mm, "end": v(5.18, 4.38) * mm});
            skLineSegment(sketch, "E6.87.0", {"start": v(7.28, 7.27) * mm, "end": v(7.5, 7.04) * mm});
            skLineSegment(sketch, "E6.87.1", {"start": v(4.9, 4.69) * mm, "end": v(7.5, 7.04) * mm});
            skLineSegment(sketch, "E6.87.2", {"start": v(4.77, 4.83) * mm, "end": v(7.28, 7.27) * mm});
            skLineSegment(sketch, "E6.87.3", {"start": v(4.77, 4.83) * mm, "end": v(4.9, 4.69) * mm});
            skLineSegment(sketch, "E6.88.0", {"start": v(6.82, 7.7) * mm, "end": v(7.05, 7.5) * mm});
            skLineSegment(sketch, "E6.88.1", {"start": v(4.62, 4.98) * mm, "end": v(7.05, 7.5) * mm});
            skLineSegment(sketch, "E6.88.2", {"start": v(4.47, 5.11) * mm, "end": v(6.82, 7.7) * mm});
            skLineSegment(sketch, "E6.88.3", {"start": v(4.47, 5.11) * mm, "end": v(4.62, 4.98) * mm});
            skLineSegment(sketch, "E6.89.0", {"start": v(6.34, 8.1) * mm, "end": v(6.58, 7.9) * mm});
            skLineSegment(sketch, "E6.89.1", {"start": v(4.3, 5.25) * mm, "end": v(6.58, 7.9) * mm});
            skLineSegment(sketch, "E6.89.2", {"start": v(4.15, 5.38) * mm, "end": v(6.34, 8.1) * mm});
            skLineSegment(sketch, "E6.89.3", {"start": v(4.15, 5.38) * mm, "end": v(4.3, 5.25) * mm});
            skLineSegment(sketch, "E6.90.0", {"start": v(5.82, 8.48) * mm, "end": v(6.08, 8.3) * mm});
            skLineSegment(sketch, "E6.90.1", {"start": v(3.97, 5.5) * mm, "end": v(6.08, 8.3) * mm});
            skLineSegment(sketch, "E6.90.2", {"start": v(3.81, 5.62) * mm, "end": v(5.82, 8.48) * mm});
            skLineSegment(sketch, "E6.90.3", {"start": v(3.81, 5.62) * mm, "end": v(3.97, 5.5) * mm});
            skLineSegment(sketch, "E6.91.0", {"start": v(5.3, 8.82) * mm, "end": v(5.55, 8.65) * mm});
            skLineSegment(sketch, "E6.91.1", {"start": v(3.63, 5.73) * mm, "end": v(5.55, 8.65) * mm});
            skLineSegment(sketch, "E6.91.2", {"start": v(3.46, 5.84) * mm, "end": v(5.3, 8.82) * mm});
            skLineSegment(sketch, "E6.91.3", {"start": v(3.46, 5.84) * mm, "end": v(3.63, 5.73) * mm});
            skLineSegment(sketch, "E6.92.0", {"start": v(4.74, 9.13) * mm, "end": v(5, 8.98) * mm});
            skLineSegment(sketch, "E6.92.1", {"start": v(3.27, 5.94) * mm, "end": v(5, 8.98) * mm});
            skLineSegment(sketch, "E6.92.2", {"start": v(3.1, 6.03) * mm, "end": v(4.74, 9.13) * mm});
            skLineSegment(sketch, "E6.92.3", {"start": v(3.1, 6.03) * mm, "end": v(3.27, 5.94) * mm});
            skLineSegment(sketch, "E6.93.0", {"start": v(4.16, 9.4) * mm, "end": v(4.45, 9.26) * mm});
            skLineSegment(sketch, "E6.93.1", {"start": v(2.9, 6.12) * mm, "end": v(4.45, 9.26) * mm});
            skLineSegment(sketch, "E6.93.2", {"start": v(2.72, 6.2) * mm, "end": v(4.16, 9.4) * mm});
            skLineSegment(sketch, "E6.93.3", {"start": v(2.72, 6.2) * mm, "end": v(2.9, 6.12) * mm});
            skLineSegment(sketch, "E6.94.0", {"start": v(3.57, 9.63) * mm, "end": v(3.86, 9.52) * mm});
            skLineSegment(sketch, "E6.94.1", {"start": v(2.52, 6.28) * mm, "end": v(3.86, 9.52) * mm});
            skLineSegment(sketch, "E6.94.2", {"start": v(2.34, 6.36) * mm, "end": v(3.57, 9.63) * mm});
            skLineSegment(sketch, "E6.94.3", {"start": v(2.34, 6.36) * mm, "end": v(2.52, 6.28) * mm});
            skLineSegment(sketch, "E6.95.0", {"start": v(2.97, 9.83) * mm, "end": v(3.27, 9.73) * mm});
            skLineSegment(sketch, "E6.95.1", {"start": v(2.14, 6.42) * mm, "end": v(3.27, 9.73) * mm});
            skLineSegment(sketch, "E6.95.2", {"start": v(1.94, 6.48) * mm, "end": v(2.97, 9.83) * mm});
            skLineSegment(sketch, "E6.95.3", {"start": v(1.94, 6.48) * mm, "end": v(2.14, 6.42) * mm});
            skLineSegment(sketch, "E6.96.0", {"start": v(2.36, 9.98) * mm, "end": v(2.66, 9.9) * mm});
            skLineSegment(sketch, "E6.96.1", {"start": v(1.74, 6.53) * mm, "end": v(2.66, 9.9) * mm});
            skLineSegment(sketch, "E6.96.2", {"start": v(1.54, 6.58) * mm, "end": v(2.36, 9.98) * mm});
            skLineSegment(sketch, "E6.96.3", {"start": v(1.54, 6.58) * mm, "end": v(1.74, 6.53) * mm});
            skLineSegment(sketch, "E6.97.0", {"start": v(1.74, 10.1) * mm, "end": v(2.04, 10.05) * mm});
            skLineSegment(sketch, "E6.97.1", {"start": v(1.33, 6.62) * mm, "end": v(2.04, 10.05) * mm});
            skLineSegment(sketch, "E6.97.2", {"start": v(1.14, 6.66) * mm, "end": v(1.74, 10.1) * mm});
            skLineSegment(sketch, "E6.97.3", {"start": v(1.14, 6.66) * mm, "end": v(1.33, 6.62) * mm});
            skLineSegment(sketch, "E6.98.0", {"start": v(1.1, 10.18) * mm, "end": v(1.42, 10.14) * mm});
            skLineSegment(sketch, "E6.98.1", {"start": v(0.93, 6.68) * mm, "end": v(1.42, 10.14) * mm});
            skLineSegment(sketch, "E6.98.2", {"start": v(0.73, 6.7) * mm, "end": v(1.1, 10.18) * mm});
            skLineSegment(sketch, "E6.98.3", {"start": v(0.73, 6.7) * mm, "end": v(0.93, 6.68) * mm});
            skLineSegment(sketch, "E6.99.0", {"start": v(0.48, 10.22) * mm, "end": v(0.79, 10.2) * mm});
            skLineSegment(sketch, "E6.99.1", {"start": v(0.51, 6.72) * mm, "end": v(0.79, 10.2) * mm});
            skLineSegment(sketch, "E6.99.2", {"start": v(0.31, 6.73) * mm, "end": v(0.48, 10.22) * mm});
            skLineSegment(sketch, "E6.99.3", {"start": v(0.31, 6.73) * mm, "end": v(0.51, 6.72) * mm});
            skPoint(sketch, "E6.center", {"position": v(0.15, 0.15) * mm});
            skSolve(sketch);
        }
        {
            var Q0;
            Q0=makeQuery(id+"F0.imprint","IMPRINT",FACE,{"disambiguationData":[TD([[makeQuery(id+"F0.imprint","IMPRINT",EDGE,{"derivedFrom":sQuery(id+"F0.wireOp",EDGE,"E0")}),-1.0]])]});
            extrude(context, id + "F1", {"entities" : qUnion([Q0]), "depth" : .22 * mm});
        }
    });
